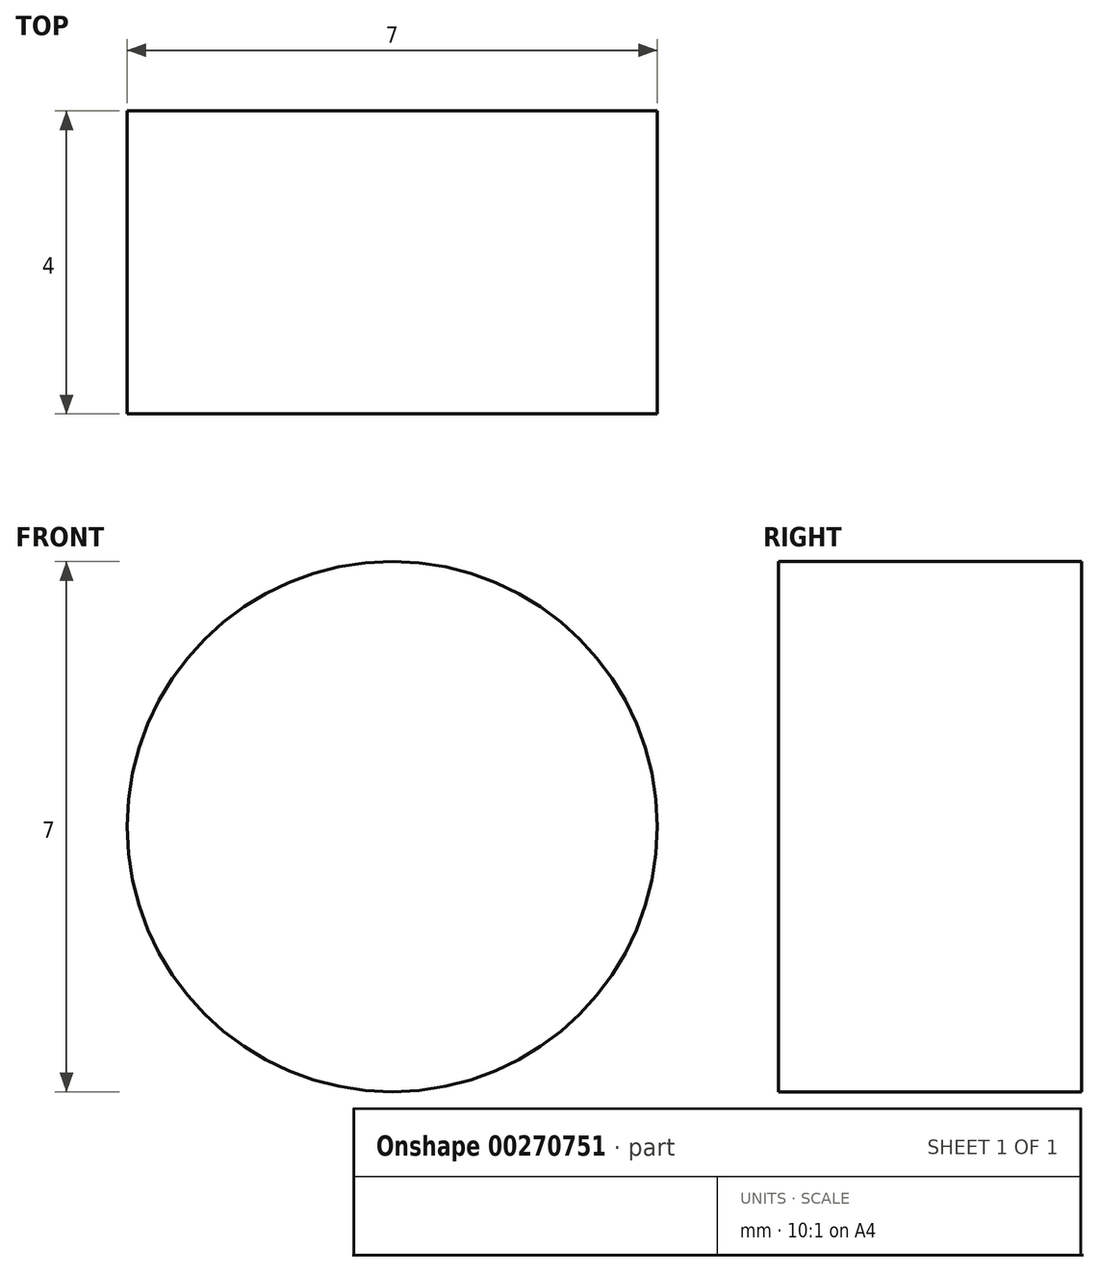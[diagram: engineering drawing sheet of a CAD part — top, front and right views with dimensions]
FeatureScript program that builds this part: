
annotation { "Feature Type Name" : "Feature", "Feature Type Description" : "" }
export const myFeature = defineFeature(function(context is Context, id is Id, definition is map)
    precondition{}
    {
        {
            var Q0;
            Q0=qCreatedBy(makeId("Front.planeOp"),FACE);
            var sketch = newSketch(context, id + "F0", { "sketchPlane" : qUnion([Q0])});
            skCircle(sketch, "E0", {"center": v(0, 0) * mm, "radius": 3.5 * mm});
            skSolve(sketch);
        }
        {
            var Q0;
            Q0 = qSketchRegion(id + "F0", true);
            extrude(context, id + "F1", {"entities" : qUnion([Q0]), "depth" : 4 * mm});
        }
    });
